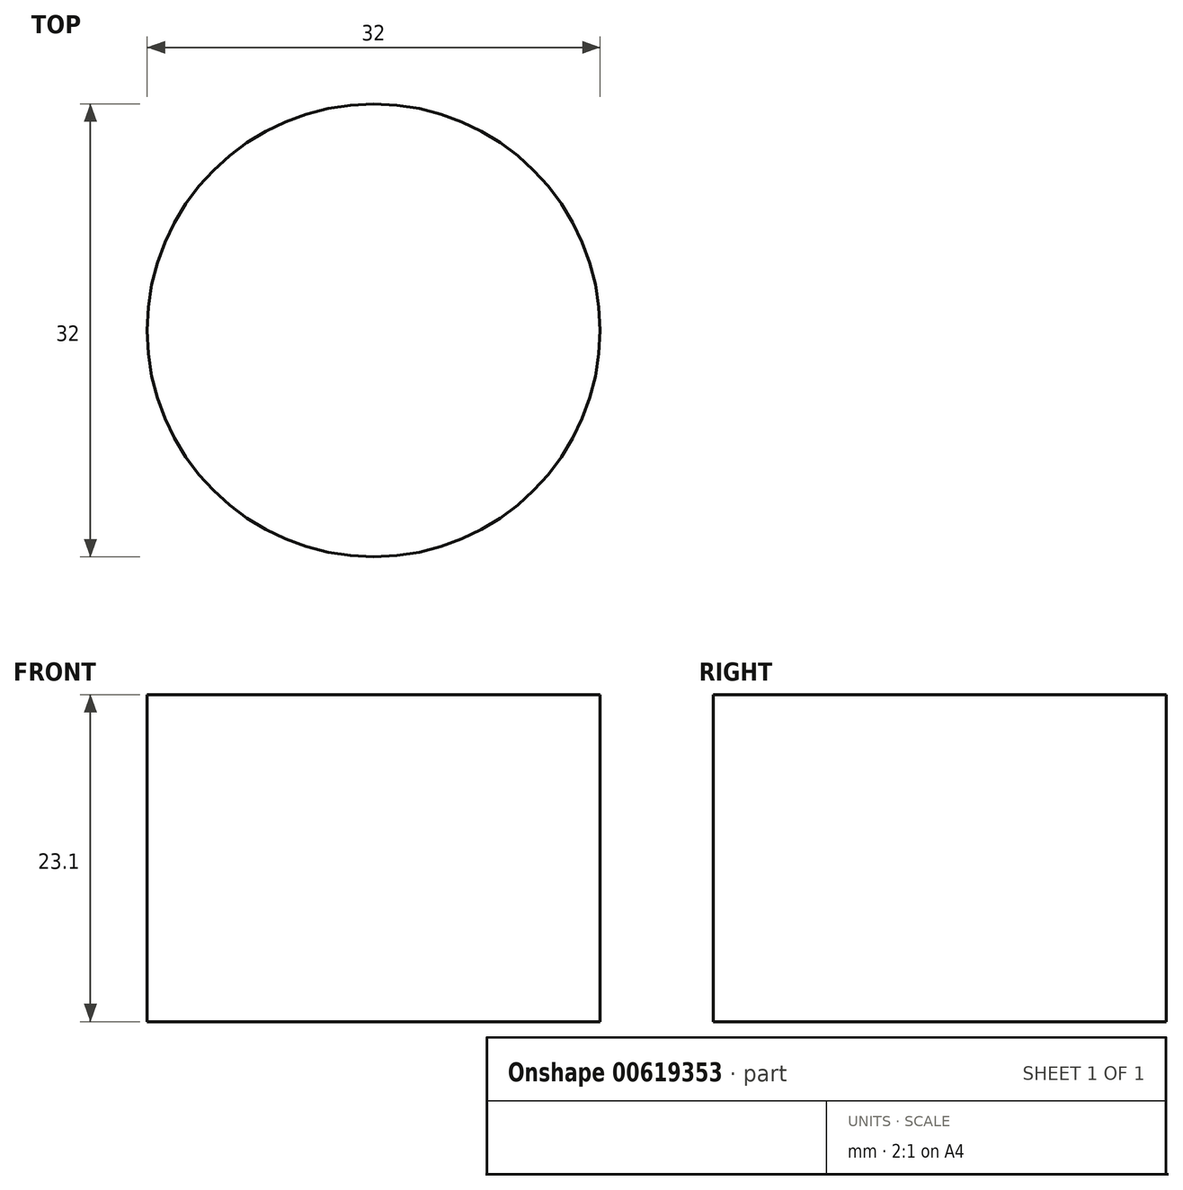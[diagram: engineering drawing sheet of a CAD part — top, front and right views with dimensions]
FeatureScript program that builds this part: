
annotation { "Feature Type Name" : "Feature", "Feature Type Description" : "" }
export const myFeature = defineFeature(function(context is Context, id is Id, definition is map)
    precondition{}
    {
        {
            var Q0;
            Q0=qCreatedBy(makeId("Top.planeOp"),FACE);
            var sketch = newSketch(context, id + "F0", { "sketchPlane" : qUnion([Q0])});
            skCircle(sketch, "E0", {"center": v(0, 0) * mm, "radius": 16 * mm});
            skSolve(sketch);
        }
        {
            var Q0;
            Q0=makeQuery(id+"F0.imprint","IMPRINT",FACE,{"disambiguationData":[TD([[makeQuery(id+"F0.imprint","IMPRINT",EDGE,{"derivedFrom":sQuery(id+"F0.wireOp",EDGE,"E0")}),1.0]])]});
            extrude(context, id + "F1", {"entities" : qUnion([Q0]), "oppositeDirection" : true, "depth" : 23.1 * mm, "offsetDistance" : 25 * mm});
        }
    });
